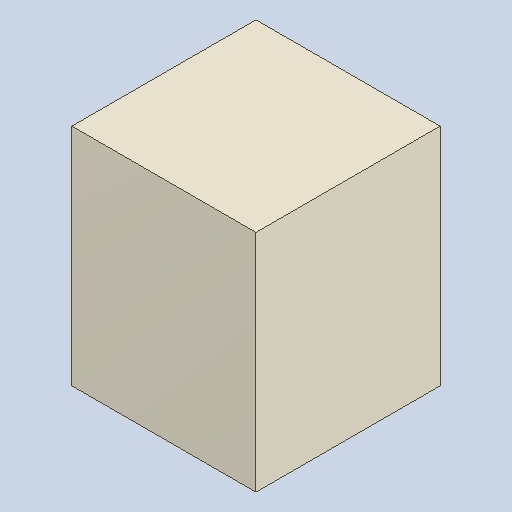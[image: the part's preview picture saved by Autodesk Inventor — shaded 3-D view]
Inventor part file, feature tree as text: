
AUTODESK INVENTOR PART (.ipt)
format: ipt  version: 2023.4 (Build 274418000, 418)  size: 82,944 bytes
history: native  units: mm
features: extrude x1
ambient origin geometry x8: Origin, YZ Plane, XZ Plane, XY Plane, X Axis, Y Axis, Z Axis, Center Point
bodies: Solid1 (feature_tree)
feature tree (1):
  extrude  "Extruded_12"  [1 undecoded]
note: 1 required parameter value undecoded (feature->parameter linkage not recoverable at this tier; creation-order binding heuristic only, values carry confidence <= 0.55)
